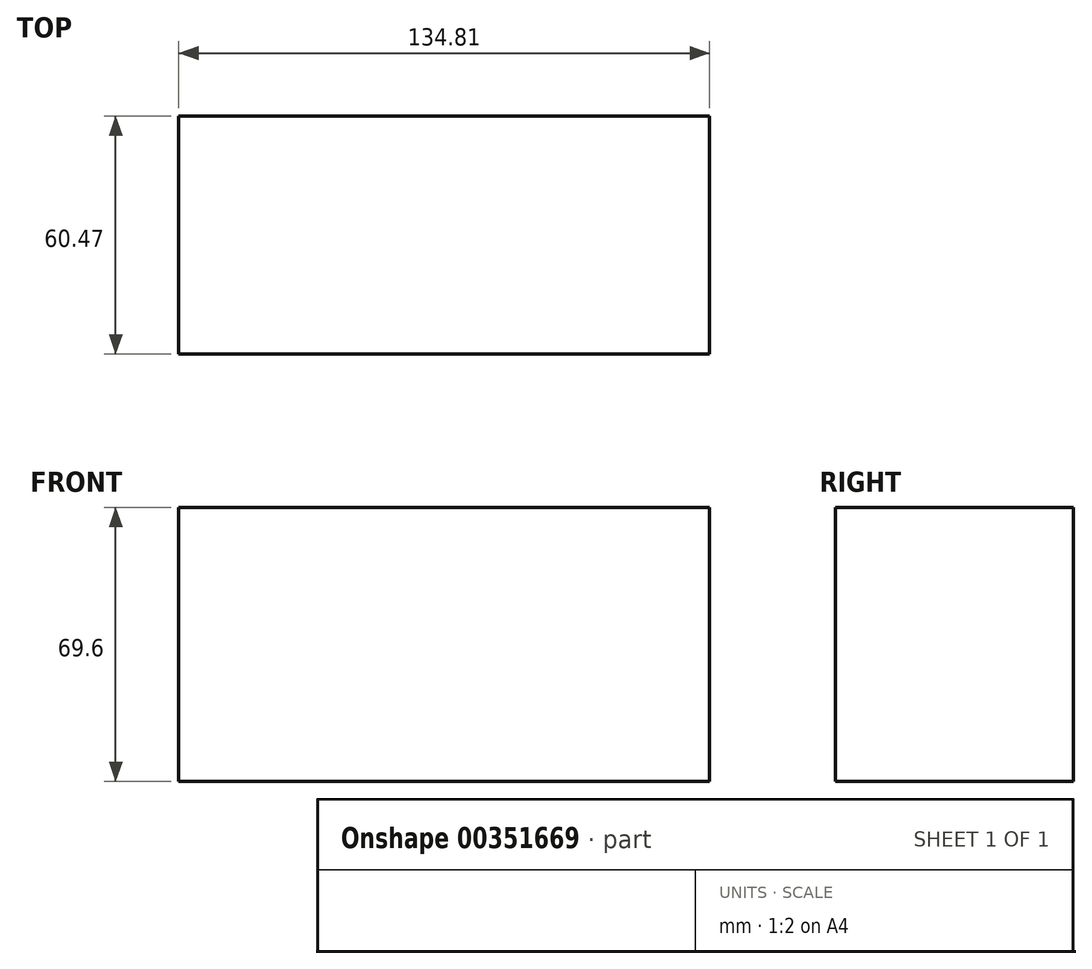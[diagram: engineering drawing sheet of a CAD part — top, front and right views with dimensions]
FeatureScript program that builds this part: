
annotation { "Feature Type Name" : "Feature", "Feature Type Description" : "" }
export const myFeature = defineFeature(function(context is Context, id is Id, definition is map)
    precondition{}
    {
        {
            var Q0;
            Q0=qCreatedBy(makeId("Top.planeOp"),FACE);
            var sketch = newSketch(context, id + "F0", { "sketchPlane" : qUnion([Q0])});
            skLineSegment(sketch, "E0.bottom", {"start": v(-68.07, 28.9) * mm, "end": v(66.74, 28.9) * mm});
            skLineSegment(sketch, "E0.top", {"start": v(-68.07, -31.58) * mm, "end": v(66.74, -31.58) * mm});
            skLineSegment(sketch, "E0.left", {"start": v(-68.07, 28.9) * mm, "end": v(-68.07, -31.58) * mm});
            skLineSegment(sketch, "E0.right", {"start": v(66.74, 28.9) * mm, "end": v(66.74, -31.58) * mm});
            skSolve(sketch);
        }
        {
            var Q0;
            Q0 = qSketchRegion(id + "F0", true);
            extrude(context, id + "F1", {"entities" : qUnion([Q0]), "depth" : 69.6 * mm});
        }
    });
